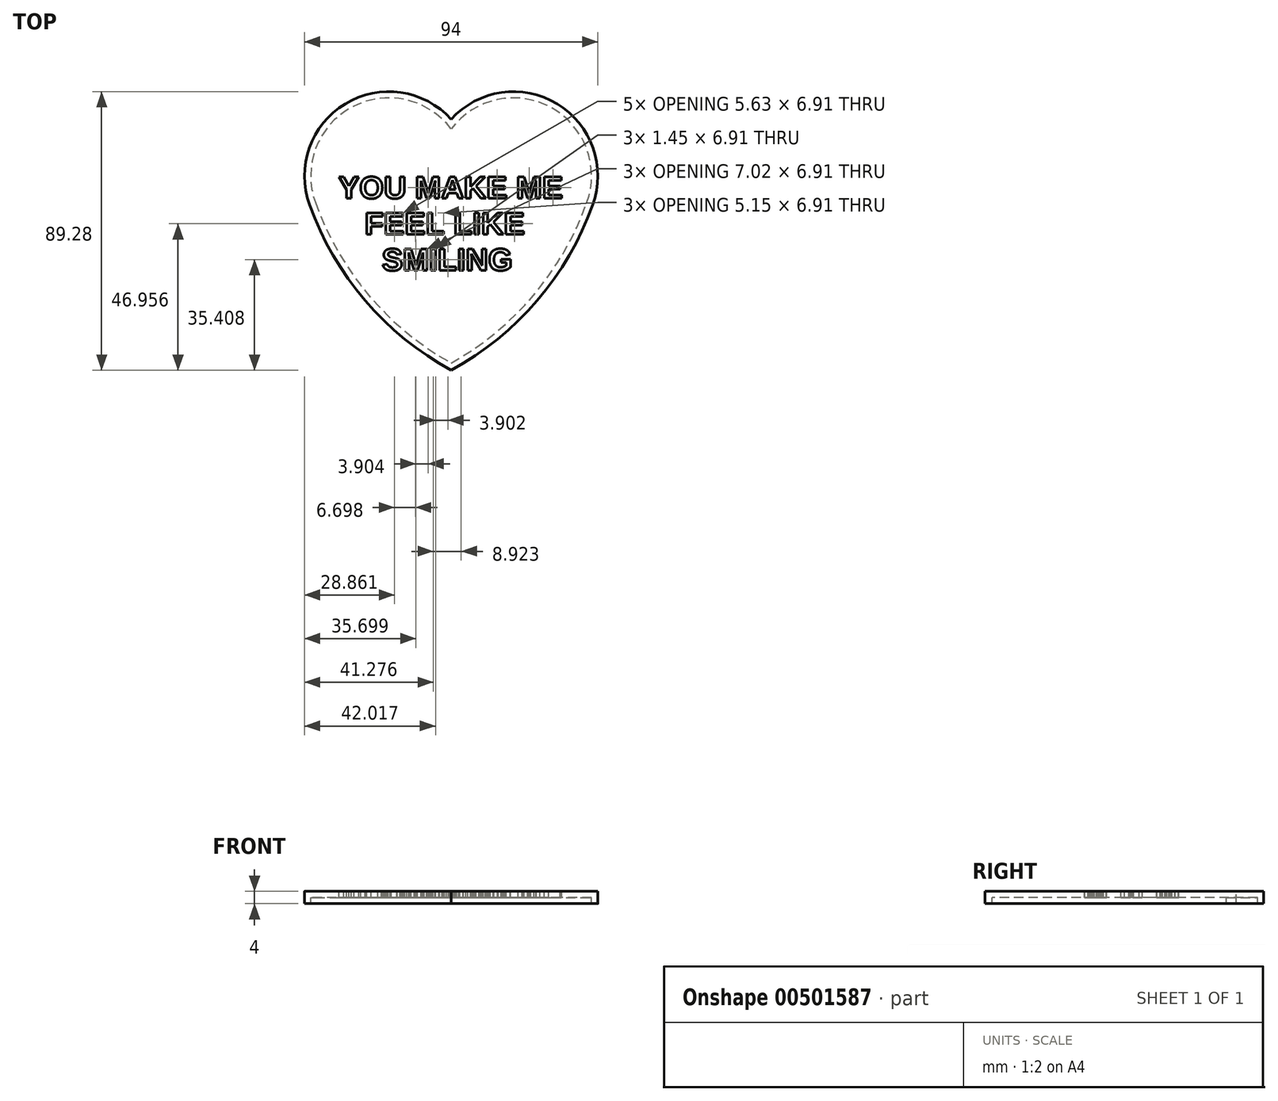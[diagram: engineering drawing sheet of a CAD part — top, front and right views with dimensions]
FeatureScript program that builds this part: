
annotation { "Feature Type Name" : "Feature", "Feature Type Description" : "" }
export const myFeature = defineFeature(function(context is Context, id is Id, definition is map)
    precondition{}
    {
        {
            var Q0;
            Q0=qCreatedBy(makeId("Top.planeOp"),FACE);
            var sketch = newSketch(context, id + "F0", { "sketchPlane" : qUnion([Q0])});
            skArc(sketch, "E0", {"start": v(-43.47, 1.39) * mm, "mid": v(-26.4, -28.25) * mm, "end": v(0, -50) * mm});
            skArc(sketch, "E1", {"start": v(0, 25) * mm, "mid": v(-31.93, 31.97) * mm, "end": v(-43.47, 1.39) * mm});
            skArc(sketch, "E2.MirrorCS", {"start": v(0, 25) * mm, "mid": v(31.93, 31.97) * mm, "end": v(43.47, 1.39) * mm});
            skArc(sketch, "E3.MirrorCS", {"start": v(43.47, 1.39) * mm, "mid": v(26.4, -28.25) * mm, "end": v(0, -50) * mm});
            skArc(sketch, "E4.0", {"start": v(0, 28.14) * mm, "mid": v(-33.98, 33.1) * mm, "end": v(-45.35, 0.7) * mm});
            skArc(sketch, "E5.0", {"start": v(0, 28.14) * mm, "mid": v(33.98, 33.1) * mm, "end": v(45.35, 0.7) * mm});
            skArc(sketch, "E6.0", {"start": v(45.35, 0.71) * mm, "mid": v(27.56, -29.97) * mm, "end": v(0, -52.28) * mm});
            skArc(sketch, "E7.0", {"start": v(-45.35, 0.71) * mm, "mid": v(-27.56, -29.97) * mm, "end": v(0, -52.28) * mm});
            skSolve(sketch);
        }
        {
            var Q0;
            Q0=qSketchRegion(id+"F0",true);
            extrude(context, id + "F1", {"entities" : qUnion([Q0]), "oppositeDirection" : true, "depth" : 2 * mm});
        }
        {
            var Q0;
            Q0=qCreatedBy(makeId("Top.planeOp"),FACE);
            var sketch = newSketch(context, id + "F2", { "sketchPlane" : qUnion([Q0])});
            skArc(sketch, "E8.0", {"start": v(0, 28.14) * mm, "mid": v(-33.98, 33.1) * mm, "end": v(-45.35, 0.7) * mm});
            skArc(sketch, "E9.0", {"start": v(0, 28.14) * mm, "mid": v(33.98, 33.1) * mm, "end": v(45.35, 0.7) * mm});
            skArc(sketch, "E10.0", {"start": v(45.35, 0.71) * mm, "mid": v(27.56, -29.97) * mm, "end": v(0, -52.28) * mm});
            skArc(sketch, "E11.0", {"start": v(-45.35, 0.71) * mm, "mid": v(-27.56, -29.97) * mm, "end": v(0, -52.28) * mm});
            skSolve(sketch);
        }
        {
            var Q0;
            Q0 = qSketchRegion(id + "F2", true);
            extrude(context, id + "F3", {"entities" : qUnion([Q0]), "operationType" : NewBodyOperationType.ADD, "depth" : 2 * mm});
        }
        {
            var Q0;
            Q0=makeQuery(id+"F3.opExtrude","CAP_FACE",FACE,{"disambiguationData":[OSD([sQuery(id+"F2.wireOp",EDGE,"E8.0"),sQuery(id+"F2.wireOp",EDGE,"E9.0"),sQuery(id+"F2.wireOp",EDGE,"E10.0"),sQuery(id+"F2.wireOp",EDGE,"E11.0")])],"isStart":false});
            var sketch = newSketch(context, id + "F4", { "sketchPlane" : qUnion([Q0])});
            skText(sketch, "E12", { "text": "YOU MAKE ME   \n   FEEL LIKE \n     SMILING", "fontName": "Arimo-Bold.ttf"});
            const initialGuessF4  = {"E12": [-0.03613, 0.00277, 1, 0, 0.00723]};
            skSetInitialGuess(sketch, initialGuessF4);
            skSolve(sketch);
        }
        {
            var Q0;
            Q0 = qSketchRegion(id + "F4", true);
            extrude(context, id + "F5", {"entities" : qUnion([Q0]), "operationType" : NewBodyOperationType.REMOVE, "oppositeDirection" : true, "depth" : 2 * mm});
        }
    });
